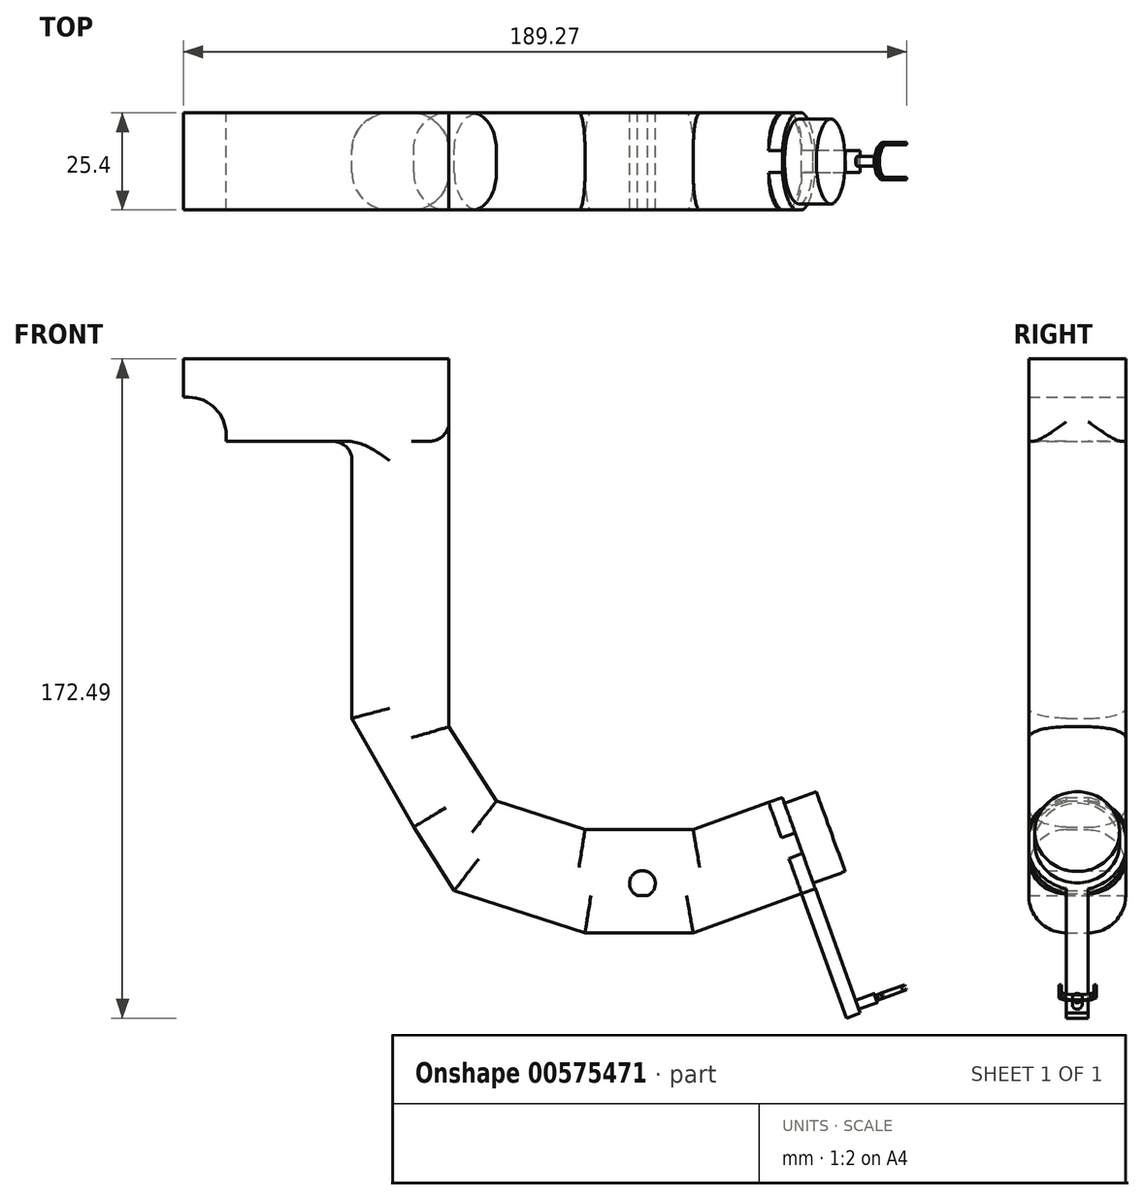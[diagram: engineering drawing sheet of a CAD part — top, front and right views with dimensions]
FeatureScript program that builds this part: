
annotation { "Feature Type Name" : "Feature", "Feature Type Description" : "" }
export const myFeature = defineFeature(function(context is Context, id is Id, definition is map)
    precondition{}
    {
        {
            var Q0;
            Q0=qCreatedBy(makeId("Front.planeOp"),FACE);
            var sketch = newSketch(context, id + "F0", { "sketchPlane" : qUnion([Q0])});
            skLineSegment(sketch, "E0", {"start": v(-89.33, 80.85) * mm, "end": v(-89.33, 8.34) * mm});
            skLineSegment(sketch, "E1", {"start": v(-89.33, 8.34) * mm, "end": v(-73.15, -20.13) * mm});
            skLineSegment(sketch, "E2", {"start": v(-73.15, -20.13) * mm, "end": v(-62.53, -36.72) * mm});
            skLineSegment(sketch, "E3", {"start": v(-62.53, -36.72) * mm, "end": v(-28.32, -47.84) * mm});
            skLineSegment(sketch, "E4", {"start": v(-28.32, -47.84) * mm, "end": v(0, -47.84) * mm});
            skLineSegment(sketch, "E5", {"start": v(0, -47.84) * mm, "end": v(28.41, -37.58) * mm});
            skLineSegment(sketch, "E6", {"start": v(28.41, -37.58) * mm, "end": v(19.78, -13.69) * mm});
            skLineSegment(sketch, "E7", {"start": v(19.78, -13.69) * mm, "end": v(0, -20.83) * mm});
            skLineSegment(sketch, "E8", {"start": v(0, -20.83) * mm, "end": v(-28.32, -20.83) * mm});
            skLineSegment(sketch, "E9", {"start": v(-28.32, -20.83) * mm, "end": v(-51.5, -13.3) * mm});
            skLineSegment(sketch, "E10", {"start": v(-51.5, -13.3) * mm, "end": v(-63.93, 6.11) * mm});
            skLineSegment(sketch, "E11", {"start": v(-63.93, 6.11) * mm, "end": v(-63.93, 80.85) * mm});
            skLineSegment(sketch, "E12", {"start": v(-63.93, 80.85) * mm, "end": v(-89.33, 80.85) * mm});
            skSolve(sketch);
        }
        {
            var Q0;
            Q0=makeQuery(id+"F0.imprint","IMPRINT",FACE,{"disambiguationData":[TD([[makeQuery(id+"F0.imprint","IMPRINT",EDGE,{"derivedFrom":sQuery(id+"F0.wireOp",EDGE,"E0")}),1.0]])]});
            extrude(context, id + "F1", {"entities" : qUnion([Q0]), "depth" : 12.7 * mm, "offsetDistance" : 25.4 * mm, "hasSecondDirection" : true, "secondDirectionOppositeDirection" : true, "secondDirectionDepth" : 12.7 * mm});
        }
        {
            var Q0;
            Q0=makeQuery(id+"F1.opExtrude","SWEPT_FACE",FACE,{"disambiguationData":[OSD([sQuery(id+"F0.wireOp",EDGE,"E6")])]});
            var sketch = newSketch(context, id + "F2", { "sketchPlane" : qUnion([Q0])});
            skCircle(sketch, "E13", {"center": v(0, -32.3) * mm, "radius": 11.1 * mm});
            skSolve(sketch);
        }
        {
            var Q0;
            Q0=makeQuery(id+"F1.opExtrude","CAP_EDGE",EDGE,{"disambiguationData":[OSD([sQuery(id+"F0.wireOp",EDGE,"E11")])],"isStart":false});
            var Q1;
            Q1=makeQuery(id+"F1.opExtrude","CAP_EDGE",EDGE,{"disambiguationData":[OSD([sQuery(id+"F0.wireOp",EDGE,"E9")])],"isStart":false});
            var Q2;
            Q2=makeQuery(id+"F1.opExtrude","CAP_EDGE",EDGE,{"disambiguationData":[OSD([sQuery(id+"F0.wireOp",EDGE,"E8")])],"isStart":false});
            var Q3;
            Q3=makeQuery(id+"F1.opExtrude","CAP_EDGE",EDGE,{"disambiguationData":[OSD([sQuery(id+"F0.wireOp",EDGE,"E7")])],"isStart":false});
            var Q4;
            Q4=makeQuery(id+"F1.opExtrude","CAP_EDGE",EDGE,{"disambiguationData":[OSD([sQuery(id+"F0.wireOp",EDGE,"E10")])],"isStart":false});
            var Q5;
            Q5=makeQuery(id+"F1.opExtrude","CAP_EDGE",EDGE,{"disambiguationData":[OSD([sQuery(id+"F0.wireOp",EDGE,"E0")])],"isStart":false});
            var Q6;
            Q6=makeQuery(id+"F1.opExtrude","CAP_EDGE",EDGE,{"disambiguationData":[OSD([sQuery(id+"F0.wireOp",EDGE,"E1")])],"isStart":false});
            var Q7;
            Q7=makeQuery(id+"F1.opExtrude","CAP_EDGE",EDGE,{"disambiguationData":[OSD([sQuery(id+"F0.wireOp",EDGE,"E2")])],"isStart":false});
            var Q8;
            Q8=makeQuery(id+"F1.opExtrude","CAP_EDGE",EDGE,{"disambiguationData":[OSD([sQuery(id+"F0.wireOp",EDGE,"E3")])],"isStart":false});
            var Q9;
            Q9=makeQuery(id+"F1.opExtrude","CAP_EDGE",EDGE,{"disambiguationData":[OSD([sQuery(id+"F0.wireOp",EDGE,"E4")])],"isStart":false});
            var Q10;
            Q10=makeQuery(id+"F1.opExtrude","CAP_EDGE",EDGE,{"disambiguationData":[OSD([sQuery(id+"F0.wireOp",EDGE,"E5")])],"isStart":false});
            var Q11;
            Q11=makeQuery(id+"F1.opExtrude","CAP_EDGE",EDGE,{"disambiguationData":[OSD([sQuery(id+"F0.wireOp",EDGE,"E9")])],"isStart":true});
            var Q12;
            Q12=makeQuery(id+"F1.opExtrude","CAP_EDGE",EDGE,{"disambiguationData":[OSD([sQuery(id+"F0.wireOp",EDGE,"E8")])],"isStart":true});
            var Q13;
            Q13=makeQuery(id+"F1.opExtrude","CAP_EDGE",EDGE,{"disambiguationData":[OSD([sQuery(id+"F0.wireOp",EDGE,"E7")])],"isStart":true});
            var Q14;
            Q14=makeQuery(id+"F1.opExtrude","CAP_EDGE",EDGE,{"disambiguationData":[OSD([sQuery(id+"F0.wireOp",EDGE,"E11")])],"isStart":true});
            var Q15;
            Q15=makeQuery(id+"F1.opExtrude","CAP_EDGE",EDGE,{"disambiguationData":[OSD([sQuery(id+"F0.wireOp",EDGE,"E10")])],"isStart":true});
            var Q16;
            Q16=makeQuery(id+"F1.opExtrude","CAP_EDGE",EDGE,{"disambiguationData":[OSD([sQuery(id+"F0.wireOp",EDGE,"E1")])],"isStart":true});
            var Q17;
            Q17=makeQuery(id+"F1.opExtrude","CAP_EDGE",EDGE,{"disambiguationData":[OSD([sQuery(id+"F0.wireOp",EDGE,"E0")])],"isStart":true});
            var Q18;
            Q18=makeQuery(id+"F1.opExtrude","CAP_EDGE",EDGE,{"disambiguationData":[OSD([sQuery(id+"F0.wireOp",EDGE,"E5")])],"isStart":true});
            var Q19;
            Q19=makeQuery(id+"F1.opExtrude","CAP_EDGE",EDGE,{"disambiguationData":[OSD([sQuery(id+"F0.wireOp",EDGE,"E4")])],"isStart":true});
            var Q20;
            Q20=makeQuery(id+"F1.opExtrude","CAP_EDGE",EDGE,{"disambiguationData":[OSD([sQuery(id+"F0.wireOp",EDGE,"E3")])],"isStart":true});
            fillet(context, id + "F3", {"entities" : qUnion([Q0, Q1, Q2, Q3, Q4, Q5, Q6, Q7, Q8, Q9, Q10, Q11, Q12, Q13, Q14, Q15, Q16, Q17, Q18, Q19, Q20]), "radius" : 9.8 * mm, "tangentPropagation" : true, "allowEdgeOverflow" : false});
        }
        {
            var Q0;
            Q0=makeQuery(id+"F2.imprint","IMPRINT",FACE,{"disambiguationData":[TD([[makeQuery(id+"F2.imprint","IMPRINT",EDGE,{"derivedFrom":sQuery(id+"F2.wireOp",EDGE,"E13")}),1.0]])]});
            extrude(context, id + "F4", {"entities" : qUnion([Q0]), "operationType" : NewBodyOperationType.ADD, "depth" : 12.7 * mm, "offsetDistance" : 25.4 * mm});
        }
        {
            var Q0;
            Q0=qCreatedBy(makeId("Front.planeOp"),FACE);
            var sketch = newSketch(context, id + "F5", { "sketchPlane" : qUnion([Q0])});
            skPoint(sketch, "E14.0", {"position": v(-63.93, 80.85) * mm});
            skPoint(sketch, "E15.0", {"position": v(-89.33, 80.85) * mm});
            skLineSegment(sketch, "E16", {"start": v(-63.93, 102.36) * mm, "end": v(-133.4, 102.36) * mm});
            skLineSegment(sketch, "E17", {"start": v(-133.4, 102.36) * mm, "end": v(-133.4, 92.33) * mm});
            skLineSegment(sketch, "E18", {"start": v(-133.4, 92.33) * mm, "end": v(-122.27, 92.33) * mm});
            skLineSegment(sketch, "E19", {"start": v(-122.27, 92.33) * mm, "end": v(-122.27, 80.85) * mm});
            skLineSegment(sketch, "E20", {"start": v(-122.27, 80.85) * mm, "end": v(-89.33, 80.85) * mm});
            skLineSegment(sketch, "E21", {"start": v(-63.93, 102.36) * mm, "end": v(-63.93, 80.85) * mm});
            skLineSegment(sketch, "E22", {"start": v(-63.93, 80.85) * mm, "end": v(-89.33, 80.85) * mm});
            skSolve(sketch);
        }
        {
            var Q0;
            Q0=makeQuery(id+"F5.imprint","IMPRINT",FACE,{"disambiguationData":[TD([[makeQuery(id+"F5.imprint","IMPRINT",EDGE,{"derivedFrom":sQuery(id+"F5.wireOp",EDGE,"E16")}),1.0]])]});
            extrude(context, id + "F6", {"entities" : qUnion([Q0]), "operationType" : NewBodyOperationType.ADD, "depth" : 12.7 * mm, "offsetDistance" : 25.4 * mm, "hasSecondDirection" : true, "secondDirectionOppositeDirection" : true, "secondDirectionDepth" : 12.7 * mm});
        }
        {
            var Q0;
            Q0=makeQuery(id+"F1.opExtrude","SWEPT_EDGE",EDGE,{"disambiguationData":[OSD([sQuery(id+"F0.wireOp",EDGE,"E0"),sQuery(id+"F0.wireOp",EDGE,"E12")])]});
            fillet(context, id + "F7", {"entities" : qUnion([Q0]), "radius" : 5.08 * mm, "tangentPropagation" : true, "allowEdgeOverflow" : false});
        }
        {
            var Q0;
            Q0=makeQuery(id+"F6.opExtrude","SWEPT_EDGE",EDGE,{"disambiguationData":[OSD([sQuery(id+"F5.wireOp",EDGE,"E18"),sQuery(id+"F5.wireOp",EDGE,"E19")])]});
            fillet(context, id + "F8", {"entities" : qUnion([Q0]), "radius" : 9.8 * mm, "tangentPropagation" : true, "allowEdgeOverflow" : false});
        }
        {
            var Q0;
            {var subQ0=sQuery(id+"F5.wireOp",EDGE,"E22");var subQ1=sQuery(id+"F5.wireOp",EDGE,"E21");var subQ3=sQuery(id+"F0.wireOp",EDGE,"E11");Q0=makeQuery(id+"F6.boolean.opBoolean","SPLIT",EDGE,{"disambiguationData":[TD([makeQuery(id+"F3.opFillet","BLEND_FACE",FACE,{"disambiguationData":[OSD([subQ3]),TDD([makeQuery(id+"F1.opExtrude","CAP_EDGE",EDGE,{"disambiguationData":[OSD([subQ3])],"isStart":true})])]})])],"derivedFrom":makeQuery(id+"F6.opExtrude","SWEPT_EDGE",EDGE,{"disambiguationData":[OSD([subQ1,subQ0])]})});}
            var Q1;
            {var subQ0=sQuery(id+"F5.wireOp",EDGE,"E22");var subQ1=sQuery(id+"F5.wireOp",EDGE,"E21");var subQ3=sQuery(id+"F0.wireOp",EDGE,"E11");Q1=makeQuery(id+"F6.boolean.opBoolean","SPLIT",EDGE,{"disambiguationData":[TD([makeQuery(id+"F3.opFillet","BLEND_FACE",FACE,{"disambiguationData":[OSD([subQ3]),TDD([makeQuery(id+"F1.opExtrude","CAP_EDGE",EDGE,{"disambiguationData":[OSD([subQ3])],"isStart":false})])]})])],"derivedFrom":makeQuery(id+"F6.opExtrude","SWEPT_EDGE",EDGE,{"disambiguationData":[OSD([subQ1,subQ0])]})});}
            fillet(context, id + "F9", {"entities" : qUnion([Q0, Q1]), "radius" : 5.08 * mm, "tangentPropagation" : true, "allowEdgeOverflow" : false});
        }
        {
            var Q0;
            Q0=makeQuery(id+"F6.boolean.opBoolean","MERGE",FACE,{"derivedFrom":[makeQuery(id+"F1.opExtrude","CAP_FACE",FACE,{"disambiguationData":[OSD([sQuery(id+"F0.wireOp",EDGE,"E0"),sQuery(id+"F0.wireOp",EDGE,"E1"),sQuery(id+"F0.wireOp",EDGE,"E2"),sQuery(id+"F0.wireOp",EDGE,"E3"),sQuery(id+"F0.wireOp",EDGE,"E4"),sQuery(id+"F0.wireOp",EDGE,"E5"),sQuery(id+"F0.wireOp",EDGE,"E6"),sQuery(id+"F0.wireOp",EDGE,"E7"),sQuery(id+"F0.wireOp",EDGE,"E8"),sQuery(id+"F0.wireOp",EDGE,"E9"),sQuery(id+"F0.wireOp",EDGE,"E10"),sQuery(id+"F0.wireOp",EDGE,"E11"),sQuery(id+"F0.wireOp",EDGE,"E12")])],"isStart":true}),makeQuery(id+"F6.opExtrude","CAP_FACE",FACE,{"disambiguationData":[OSD([sQuery(id+"F5.wireOp",EDGE,"E16"),sQuery(id+"F5.wireOp",EDGE,"E17"),sQuery(id+"F5.wireOp",EDGE,"E18"),sQuery(id+"F5.wireOp",EDGE,"E19"),sQuery(id+"F5.wireOp",EDGE,"E20"),sQuery(id+"F5.wireOp",EDGE,"E21"),sQuery(id+"F5.wireOp",EDGE,"E22")])],"isStart":true})]});
            var sketch = newSketch(context, id + "F10", { "sketchPlane" : qUnion([Q0])});
            skCircle(sketch, "E23", {"center": v(13.28, -34.92) * mm, "radius": 3.38 * mm});
            skSolve(sketch);
        }
        {
            var Q0;
            {var subQ0=sQuery(id+"F10.wireOp",EDGE,"E23");var subQ1=sQuery(id+"F0.wireOp",EDGE,"E4");var subQ2=makeQuery(id+"F3.opFillet","BLEND_EDGE",EDGE,{"blendedFrom":[makeQuery(id+"F1.opExtrude","CAP_EDGE",EDGE,{"disambiguationData":[OSD([subQ1])],"isStart":true}),makeQuery(id+"F1.opExtrude","CAP_FACE",FACE,{"disambiguationData":[OSD([sQuery(id+"F0.wireOp",EDGE,"E0"),sQuery(id+"F0.wireOp",EDGE,"E1"),sQuery(id+"F0.wireOp",EDGE,"E2"),sQuery(id+"F0.wireOp",EDGE,"E3"),subQ1,sQuery(id+"F0.wireOp",EDGE,"E5"),sQuery(id+"F0.wireOp",EDGE,"E6"),sQuery(id+"F0.wireOp",EDGE,"E7"),sQuery(id+"F0.wireOp",EDGE,"E8"),sQuery(id+"F0.wireOp",EDGE,"E9"),sQuery(id+"F0.wireOp",EDGE,"E10"),sQuery(id+"F0.wireOp",EDGE,"E11"),sQuery(id+"F0.wireOp",EDGE,"E12")])],"isStart":true})],"blendedInto":[makeQuery(id+"F1.opExtrude","CAP_FACE",FACE,{"disambiguationData":[OSD([sQuery(id+"F0.wireOp",EDGE,"E0"),sQuery(id+"F0.wireOp",EDGE,"E1"),sQuery(id+"F0.wireOp",EDGE,"E2"),sQuery(id+"F0.wireOp",EDGE,"E3"),subQ1,sQuery(id+"F0.wireOp",EDGE,"E5"),sQuery(id+"F0.wireOp",EDGE,"E6"),sQuery(id+"F0.wireOp",EDGE,"E7"),sQuery(id+"F0.wireOp",EDGE,"E8"),sQuery(id+"F0.wireOp",EDGE,"E9"),sQuery(id+"F0.wireOp",EDGE,"E10"),sQuery(id+"F0.wireOp",EDGE,"E11"),sQuery(id+"F0.wireOp",EDGE,"E12")])],"isStart":true})]});var subQ3=makeQuery(id+"F10.imprint","INTERSECT",VERTEX,{"disambiguationData":[OD(0.0)],"derivedFrom":[subQ2,subQ0]});Q0=makeQuery(id+"F10.imprint","IMPRINT",FACE,{"disambiguationData":[TD([[makeQuery(id+"F10.imprint","IMPRINT",EDGE,{"disambiguationData":[TD([[subQ3,-1.0]])],"derivedFrom":subQ0}),1.0]])]});}
            extrude(context, id + "F11", {"entities" : qUnion([Q0]), "operationType" : NewBodyOperationType.REMOVE, "endBound" : BoundingType.THROUGH_ALL, "oppositeDirection" : true, "depth" : 25.4 * mm, "offsetDistance" : 25.4 * mm});
        }
        {
            var Q0;
            Q0=makeQuery(id+"F1.opExtrude","SWEPT_FACE",FACE,{"disambiguationData":[OSD([sQuery(id+"F0.wireOp",EDGE,"E6")])]});
            var sketch = newSketch(context, id + "F12", { "sketchPlane" : qUnion([Q0])});
            skCircle(sketch, "E24", {"center": v(0, -32.3) * mm, "radius": 13.02 * mm});
            skSolve(sketch);
        }
        {
            var Q0;
            {var subQ1=sQuery(id+"F0.wireOp",EDGE,"E6");var subQ2=makeQuery(id+"F1.opExtrude","CAP_EDGE",EDGE,{"disambiguationData":[OSD([subQ1])],"isStart":true});Q0=makeQuery(id+"F12.imprint","IMPRINT",FACE,{"disambiguationData":[TD([[makeQuery(id+"F12.imprint","IMPRINT",EDGE,{"derivedFrom":subQ2}),1.0]])]});}
            var Q1;
            Q1=makeQuery(id+"F4.opExtrude","CAP_FACE",FACE,{"disambiguationData":[OSD([sQuery(id+"F2.wireOp",EDGE,"E13")])],"isStart":false});
            extrude(context, id + "F13", {"entities" : qUnion([Q0]), "depth" : 3.8 * mm, "endBoundEntityFace" : qUnion([Q1]), "offsetDistance" : 25.4 * mm});
        }
        {
            var Q0;
            Q0=makeQuery(id+"F13.opExtrude","CAP_FACE",FACE,{"disambiguationData":[OSD([sQuery(id+"F2.wireOp",EDGE,"E13")])],"isStart":false});
            var sketch = newSketch(context, id + "F14", { "sketchPlane" : qUnion([Q0])});
            skLineSegment(sketch, "E25", {"start": v(-2.89, -45) * mm, "end": v(-2.89, -79.61) * mm});
            skLineSegment(sketch, "E26", {"start": v(-2.89, -79.61) * mm, "end": v(2.89, -79.61) * mm});
            skLineSegment(sketch, "E27", {"start": v(2.89, -79.61) * mm, "end": v(2.89, -45) * mm});
            skSolve(sketch);
        }
        {
            var Q0;
            Q0 = qSketchRegion(id + "F14", true);
            var Q1;
            Q1=makeQuery(id+"F14.imprint","IMPRINT",FACE,{"disambiguationData":[TD([[makeQuery(id+"F14.imprint","IMPRINT",EDGE,{"derivedFrom":sQuery(id+"F14.wireOp",EDGE,"E25")}),1.0]])]});
            var Q2;
            {var subQ0=sQuery(id+"F0.wireOp",EDGE,"E5");Q2=makeQuery(id+"F3.opFillet","BLEND_VERTEX",VERTEX,{"blendedFrom":[makeQuery(id+"F1.opExtrude","CAP_EDGE",EDGE,{"disambiguationData":[OSD([subQ0])],"isStart":true}),makeQuery(id+"F1.opExtrude","SWEPT_FACE",FACE,{"disambiguationData":[OSD([subQ0])]}),makeQuery(id+"F1.opExtrude","SWEPT_FACE",FACE,{"disambiguationData":[OSD([sQuery(id+"F0.wireOp",EDGE,"E6")])]})],"blendedInto":[makeQuery(id+"F1.opExtrude","SWEPT_FACE",FACE,{"disambiguationData":[OSD([subQ0])]}),makeQuery(id+"F1.opExtrude","SWEPT_FACE",FACE,{"disambiguationData":[OSD([sQuery(id+"F0.wireOp",EDGE,"E6")])]})]});}
            extrude(context, id + "F15", {"entities" : qUnion([Q0, Q1]), "operationType" : NewBodyOperationType.ADD, "endBound" : BoundingType.UP_TO_VERTEX, "oppositeDirection" : true, "depth" : 3.8 * mm, "endBoundEntityVertex" : qUnion([Q2]), "offsetDistance" : 25.4 * mm});
        }
        {
            var Q0;
            {var subQ0=sQuery(id+"F2.wireOp",EDGE,"E13");Q0=makeQuery(id+"F15.boolean.opBoolean","MERGE",FACE,{"derivedFrom":[makeQuery(id+"F13.opExtrude","CAP_FACE",FACE,{"disambiguationData":[OSD([subQ0])],"isStart":false}),makeQuery(id+"F15.opExtrude","CAP_FACE",FACE,{"disambiguationData":[OSD([sQuery(id+"F0.wireOp",EDGE,"E5"),sQuery(id+"F0.wireOp",EDGE,"E6"),subQ0,sQuery(id+"F14.wireOp",EDGE,"E25"),sQuery(id+"F14.wireOp",EDGE,"E26"),sQuery(id+"F14.wireOp",EDGE,"E27")])],"isStart":true})]});}
            var sketch = newSketch(context, id + "F16", { "sketchPlane" : qUnion([Q0])});
            skCircle(sketch, "E28", {"center": v(0, -77.26) * mm, "radius": 1.27 * mm});
            skSolve(sketch);
        }
        {
            var Q0;
            Q0=makeQuery(id+"F16.imprint","IMPRINT",FACE,{"disambiguationData":[TD([[makeQuery(id+"F16.imprint","IMPRINT",EDGE,{"derivedFrom":sQuery(id+"F16.wireOp",EDGE,"E28")}),1.0]])]});
            extrude(context, id + "F17", {"entities" : qUnion([Q0]), "operationType" : NewBodyOperationType.ADD, "depth" : 5.13 * mm, "offsetDistance" : 25.4 * mm});
        }
        {
            var Q0;
            Q0=makeQuery(id+"F15.opExtrude","SWEPT_FACE",FACE,{"disambiguationData":[OSD([sQuery(id+"F14.wireOp",EDGE,"E26")])]});
            var sketch = newSketch(context, id + "F18", { "sketchPlane" : qUnion([Q0])});
            skLineSegment(sketch, "E29.0", {"start": v(22.9, 1.27) * mm, "end": v(22.9, -1.27) * mm});
            skLineSegment(sketch, "E30", {"start": v(22.9, -1.27) * mm, "end": v(23.57, -3.57) * mm});
            skLineSegment(sketch, "E31", {"start": v(23.57, -3.57) * mm, "end": v(24.96, -4.95) * mm});
            skLineSegment(sketch, "E32", {"start": v(24.96, -4.95) * mm, "end": v(31.22, -4.95) * mm});
            skLineSegment(sketch, "E33", {"start": v(31.22, -4.95) * mm, "end": v(31.22, -4.34) * mm});
            skLineSegment(sketch, "E34", {"start": v(31.22, -4.34) * mm, "end": v(25.24, -4.34) * mm});
            skLineSegment(sketch, "E35", {"start": v(25.24, -4.34) * mm, "end": v(24.32, -3.47) * mm});
            skLineSegment(sketch, "E36", {"start": v(24.32, -3.47) * mm, "end": v(23.68, -1.27) * mm});
            skLineSegment(sketch, "E37", {"start": v(23.68, -1.27) * mm, "end": v(23.68, 1.25) * mm});
            skLineSegment(sketch, "E38", {"start": v(23.68, 1.25) * mm, "end": v(24.1, 3.11) * mm});
            skLineSegment(sketch, "E39", {"start": v(24.1, 3.11) * mm, "end": v(25.04, 4.16) * mm});
            skLineSegment(sketch, "E40", {"start": v(25.04, 4.16) * mm, "end": v(31.22, 4.16) * mm});
            skLineSegment(sketch, "E41", {"start": v(31.22, 4.16) * mm, "end": v(31.22, 4.76) * mm});
            skLineSegment(sketch, "E42", {"start": v(31.22, 4.76) * mm, "end": v(24.7, 4.76) * mm});
            skLineSegment(sketch, "E43", {"start": v(24.7, 4.76) * mm, "end": v(23.43, 3.46) * mm});
            skLineSegment(sketch, "E44", {"start": v(23.43, 3.46) * mm, "end": v(22.9, 1.27) * mm});
            skSolve(sketch);
        }
        {
            var Q0;
            Q0=makeQuery(id+"F18.imprint","IMPRINT",FACE,{"disambiguationData":[TD([[makeQuery(id+"F18.imprint","IMPRINT",EDGE,{"derivedFrom":sQuery(id+"F18.wireOp",EDGE,"E29.0")}),1.0]])]});
            extrude(context, id + "F19", {"entities" : qUnion([Q0]), "operationType" : NewBodyOperationType.ADD, "oppositeDirection" : true, "depth" : 3.05 * mm, "offsetDistance" : 25.4 * mm, "hasSecondDirection" : true, "secondDirectionOppositeDirection" : true, "secondDirectionDepth" : 1.63 * mm});
        }
        {
            var Q0;
            Q0=makeQuery(id+"F19.opExtrude","SWEPT_FACE",FACE,{"disambiguationData":[OSD([sQuery(id+"F18.wireOp",EDGE,"E32")])]});
            var sketch = newSketch(context, id + "F20", { "sketchPlane" : qUnion([Q0])});
            skCircle(sketch, "E45", {"center": v(-55.21, -62.24) * mm, "radius": 0.55 * mm});
            skSolve(sketch);
        }
        {
            var Q0;
            Q0=makeQuery(id+"F20.imprint","IMPRINT",FACE,{"disambiguationData":[TD([[makeQuery(id+"F20.imprint","IMPRINT",EDGE,{"derivedFrom":sQuery(id+"F20.wireOp",EDGE,"E45")}),1.0]])]});
            extrude(context, id + "F21", {"entities" : qUnion([Q0]), "operationType" : NewBodyOperationType.REMOVE, "endBound" : BoundingType.THROUGH_ALL, "oppositeDirection" : true, "depth" : 25.4 * mm, "offsetDistance" : 25.4 * mm});
        }
    });
